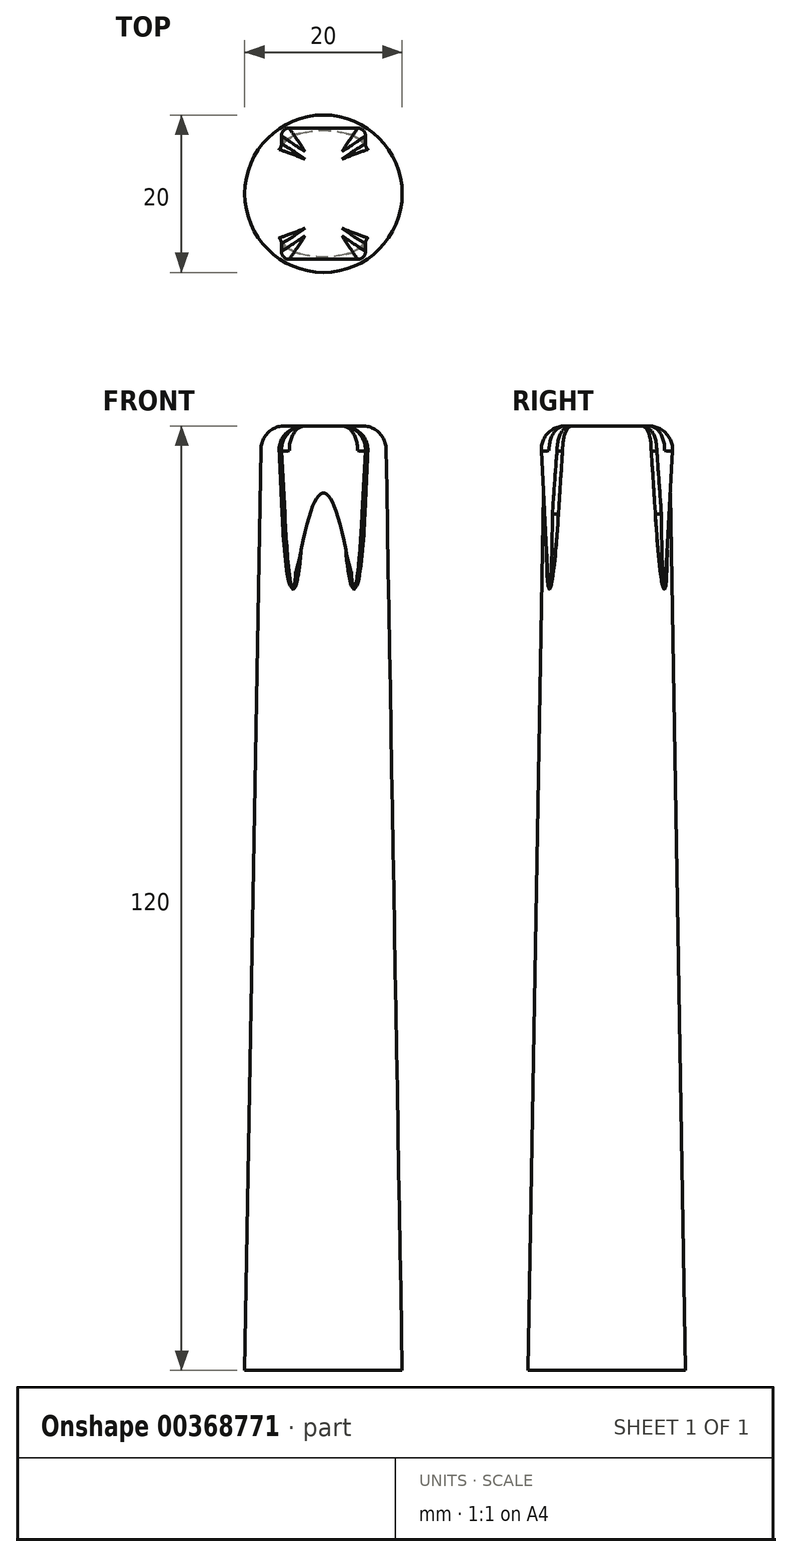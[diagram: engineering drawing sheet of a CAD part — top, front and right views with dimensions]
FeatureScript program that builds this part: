
annotation { "Feature Type Name" : "Feature", "Feature Type Description" : "" }
export const myFeature = defineFeature(function(context is Context, id is Id, definition is map)
    precondition{}
    {
        {
            var Q0;
            Q0=qCreatedBy(makeId("Top.planeOp"),FACE);
            var sketch = newSketch(context, id + "F0", { "sketchPlane" : qUnion([Q0])});
            skCircle(sketch, "E0", {"center": v(0, 0) * mm, "radius": 10 * mm});
            skSolve(sketch);
        }
        {
            var Q0;
            Q0 = qSketchRegion(id + "F0", true);
            extrude(context, id + "F1", {"entities" : qUnion([Q0]), "depth" : 120 * mm, "hasDraft" : true, "draftAngle" : 1 * degree, "draftPullDirection" : true});
        }
        {
            var Q0;
            Q0=makeQuery(id+"F1.opExtrude","CAP_FACE",FACE,{"disambiguationData":[OSD([sQuery(id+"F0.wireOp",EDGE,"E0")])],"isStart":false});
            var sketch = newSketch(context, id + "F2", { "sketchPlane" : qUnion([Q0])});
            skCircle(sketch, "E1.0", {"center": v(0, 0) * mm, "radius": 7.9 * mm});
            skLineSegment(sketch, "E2.bottom", {"start": v(5.5, 8.5) * mm, "end": v(-5.5, 8.5) * mm});
            skLineSegment(sketch, "E2.top", {"start": v(5.5, -8.5) * mm, "end": v(-5.5, -8.5) * mm});
            skLineSegment(sketch, "E2.left", {"start": v(5.5, 8.5) * mm, "end": v(5.5, -8.5) * mm});
            skLineSegment(sketch, "E2.right", {"start": v(-5.5, 8.5) * mm, "end": v(-5.5, -8.5) * mm});
            skSolve(sketch);
        }
        {
            var Q0;
            {var subQ5=sQuery(id+"F2.wireOp",EDGE,"E2.bottom");Q0=makeQuery(id+"F2.imprint","IMPRINT",FACE,{"disambiguationData":[TD([[makeQuery(id+"F2.imprint","IMPRINT",EDGE,{"derivedFrom":subQ5}),1.0]])]});}
            var Q1;
            {var subQ0=sQuery(id+"F2.wireOp",EDGE,"E2.right");var subQ1=sQuery(id+"F2.wireOp",EDGE,"E1.0");var subQ2=makeQuery(id+"F2.imprint","INTERSECT",VERTEX,{"disambiguationData":[OD(0.0)],"derivedFrom":[subQ1,subQ0]});Q1=makeQuery(id+"F2.imprint","IMPRINT",FACE,{"disambiguationData":[TD([[makeQuery(id+"F2.imprint","IMPRINT",EDGE,{"disambiguationData":[TD([[subQ2,1.0]])],"derivedFrom":subQ1}),1.0]])]});}
            var Q2;
            {var subQ5=sQuery(id+"F2.wireOp",EDGE,"E2.top");Q2=makeQuery(id+"F2.imprint","IMPRINT",FACE,{"disambiguationData":[TD([[makeQuery(id+"F2.imprint","IMPRINT",EDGE,{"derivedFrom":subQ5}),-1.0]])]});}
            extrude(context, id + "F3", {"entities" : qUnion([Q0, Q1, Q2]), "operationType" : NewBodyOperationType.ADD, "oppositeDirection" : true, "depth" : 25 * mm, "hasDraft" : true, "draftAngle" : 3 * degree, "draftPullDirection" : true});
        }
        {
            var Q0;
            {var subQ0=sQuery(id+"F0.wireOp",EDGE,"E0");var subQ1=sQuery(id+"F2.wireOp",EDGE,"E2.right");Q0=makeQuery(id+"F3.boolean.opBoolean","SPLIT",EDGE,{"disambiguationData":[TD([makeQuery(id+"F3.opExtrude","SWEPT_FACE",FACE,{"disambiguationData":[OSD([subQ1])]})])],"derivedFrom":makeQuery(id+"F1.opExtrude","CAP_EDGE",EDGE,{"disambiguationData":[OSD([subQ0])],"isStart":false})});}
            var Q1;
            Q1=makeQuery(id+"F3.boolean.opBoolean","MERGE",FACE,{"derivedFrom":[makeQuery(id+"F1.opExtrude","CAP_FACE",FACE,{"disambiguationData":[OSD([sQuery(id+"F0.wireOp",EDGE,"E0")])],"isStart":false}),makeQuery(id+"F3.opExtrude","CAP_FACE",FACE,{"disambiguationData":[OSD([sQuery(id+"F2.wireOp",EDGE,"E2.bottom"),sQuery(id+"F2.wireOp",EDGE,"E2.top"),sQuery(id+"F2.wireOp",EDGE,"E2.left"),sQuery(id+"F2.wireOp",EDGE,"E2.right")])],"isStart":true})]});
            fillet(context, id + "F4", {"entities" : qUnion([Q0, Q1]), "radius" : 3 * mm, "tangentPropagation" : true, "allowEdgeOverflow" : false});
        }
        {
            var Q0;
            {var subQ0=sQuery(id+"F2.wireOp",EDGE,"E2.top");var subQ1=sQuery(id+"F2.wireOp",EDGE,"E2.right");Q0=makeQuery(id+"F4.opFillet","BLEND_EDGE",EDGE,{"blendedFrom":[makeQuery(id+"F3.opExtrude","CAP_EDGE",EDGE,{"disambiguationData":[OSD([subQ0])],"isStart":true}),makeQuery(id+"F3.boolean.opBoolean","SPLIT",EDGE,{"disambiguationData":[TD([makeQuery(id+"F3.opExtrude","SWEPT_FACE",FACE,{"disambiguationData":[OSD([subQ0])]})])],"derivedFrom":makeQuery(id+"F3.opExtrude","CAP_EDGE",EDGE,{"disambiguationData":[OSD([subQ1])],"isStart":true})})],"blendedInto":[]});}
            var Q1;
            {var subQ0=sQuery(id+"F2.wireOp",EDGE,"E2.top");var subQ1=sQuery(id+"F2.wireOp",EDGE,"E2.left");Q1=makeQuery(id+"F4.opFillet","BLEND_EDGE",EDGE,{"blendedFrom":[makeQuery(id+"F3.opExtrude","CAP_EDGE",EDGE,{"disambiguationData":[OSD([subQ0])],"isStart":true}),makeQuery(id+"F3.boolean.opBoolean","SPLIT",EDGE,{"disambiguationData":[TD([makeQuery(id+"F3.opExtrude","SWEPT_FACE",FACE,{"disambiguationData":[OSD([subQ0])]})])],"derivedFrom":makeQuery(id+"F3.opExtrude","CAP_EDGE",EDGE,{"disambiguationData":[OSD([subQ1])],"isStart":true})})],"blendedInto":[]});}
            var Q2;
            {var subQ0=sQuery(id+"F2.wireOp",EDGE,"E2.bottom");var subQ2=sQuery(id+"F2.wireOp",EDGE,"E2.right");Q2=makeQuery(id+"F4.opFillet","BLEND_EDGE",EDGE,{"blendedFrom":[makeQuery(id+"F3.opExtrude","CAP_EDGE",EDGE,{"disambiguationData":[OSD([subQ0])],"isStart":true}),makeQuery(id+"F3.boolean.opBoolean","SPLIT",EDGE,{"disambiguationData":[TD([makeQuery(id+"F3.opExtrude","SWEPT_FACE",FACE,{"disambiguationData":[OSD([subQ0])]})])],"derivedFrom":makeQuery(id+"F3.opExtrude","CAP_EDGE",EDGE,{"disambiguationData":[OSD([subQ2])],"isStart":true})})],"blendedInto":[]});}
            var Q3;
            {var subQ0=sQuery(id+"F2.wireOp",EDGE,"E2.bottom");var subQ2=sQuery(id+"F2.wireOp",EDGE,"E2.left");Q3=makeQuery(id+"F4.opFillet","BLEND_EDGE",EDGE,{"blendedFrom":[makeQuery(id+"F3.opExtrude","CAP_EDGE",EDGE,{"disambiguationData":[OSD([subQ0])],"isStart":true}),makeQuery(id+"F3.boolean.opBoolean","SPLIT",EDGE,{"disambiguationData":[TD([makeQuery(id+"F3.opExtrude","SWEPT_FACE",FACE,{"disambiguationData":[OSD([subQ0])]})])],"derivedFrom":makeQuery(id+"F3.opExtrude","CAP_EDGE",EDGE,{"disambiguationData":[OSD([subQ2])],"isStart":true})})],"blendedInto":[]});}
            var Q4;
            {var subQ0=sQuery(id+"F0.wireOp",EDGE,"E0");var subQ2=sQuery(id+"F2.wireOp",EDGE,"E2.left");var subQ3=makeQuery(id+"F3.opExtrude","SWEPT_FACE",FACE,{"disambiguationData":[OSD([subQ2])]});var subQ5=sQuery(id+"F2.wireOp",EDGE,"E2.bottom");Q4=makeQuery(id+"F4.opFillet","BLEND_EDGE",EDGE,{"blendedFrom":[makeQuery(id+"F3.boolean.opBoolean","SPLIT",EDGE,{"disambiguationData":[TD([makeQuery(id+"F3.opExtrude","SWEPT_FACE",FACE,{"disambiguationData":[OSD([subQ5])]})])],"derivedFrom":makeQuery(id+"F3.opExtrude","CAP_EDGE",EDGE,{"disambiguationData":[OSD([subQ2])],"isStart":true})}),makeQuery(id+"F3.boolean.opBoolean","SPLIT",EDGE,{"disambiguationData":[TD([subQ3])],"derivedFrom":makeQuery(id+"F1.opExtrude","CAP_EDGE",EDGE,{"disambiguationData":[OSD([subQ0])],"isStart":false})})],"blendedInto":[]});}
            var Q5;
            {var subQ0=sQuery(id+"F0.wireOp",EDGE,"E0");var subQ3=sQuery(id+"F2.wireOp",EDGE,"E2.right");var subQ4=sQuery(id+"F2.wireOp",EDGE,"E2.top");var subQ6=makeQuery(id+"F3.opExtrude","SWEPT_FACE",FACE,{"disambiguationData":[OSD([subQ3])]});Q5=makeQuery(id+"F4.opFillet","BLEND_EDGE",EDGE,{"blendedFrom":[makeQuery(id+"F3.boolean.opBoolean","SPLIT",EDGE,{"disambiguationData":[TD([makeQuery(id+"F3.opExtrude","SWEPT_FACE",FACE,{"disambiguationData":[OSD([subQ4])]})])],"derivedFrom":makeQuery(id+"F3.opExtrude","CAP_EDGE",EDGE,{"disambiguationData":[OSD([subQ3])],"isStart":true})}),makeQuery(id+"F3.boolean.opBoolean","SPLIT",EDGE,{"disambiguationData":[TD([subQ6])],"derivedFrom":makeQuery(id+"F1.opExtrude","CAP_EDGE",EDGE,{"disambiguationData":[OSD([subQ0])],"isStart":false})})],"blendedInto":[]});}
            var Q6;
            {var subQ0=sQuery(id+"F0.wireOp",EDGE,"E0");var subQ2=sQuery(id+"F2.wireOp",EDGE,"E2.left");var subQ3=makeQuery(id+"F3.opExtrude","SWEPT_FACE",FACE,{"disambiguationData":[OSD([subQ2])]});var subQ5=sQuery(id+"F2.wireOp",EDGE,"E2.top");Q6=makeQuery(id+"F4.opFillet","BLEND_EDGE",EDGE,{"blendedFrom":[makeQuery(id+"F3.boolean.opBoolean","SPLIT",EDGE,{"disambiguationData":[TD([makeQuery(id+"F3.opExtrude","SWEPT_FACE",FACE,{"disambiguationData":[OSD([subQ5])]})])],"derivedFrom":makeQuery(id+"F3.opExtrude","CAP_EDGE",EDGE,{"disambiguationData":[OSD([subQ2])],"isStart":true})}),makeQuery(id+"F3.boolean.opBoolean","SPLIT",EDGE,{"disambiguationData":[TD([subQ3])],"derivedFrom":makeQuery(id+"F1.opExtrude","CAP_EDGE",EDGE,{"disambiguationData":[OSD([subQ0])],"isStart":false})})],"blendedInto":[]});}
            var Q7;
            {var subQ0=sQuery(id+"F0.wireOp",EDGE,"E0");var subQ3=sQuery(id+"F2.wireOp",EDGE,"E2.right");var subQ4=sQuery(id+"F2.wireOp",EDGE,"E2.bottom");var subQ6=makeQuery(id+"F3.opExtrude","SWEPT_FACE",FACE,{"disambiguationData":[OSD([subQ3])]});Q7=makeQuery(id+"F4.opFillet","BLEND_EDGE",EDGE,{"blendedFrom":[makeQuery(id+"F3.boolean.opBoolean","SPLIT",EDGE,{"disambiguationData":[TD([makeQuery(id+"F3.opExtrude","SWEPT_FACE",FACE,{"disambiguationData":[OSD([subQ4])]})])],"derivedFrom":makeQuery(id+"F3.opExtrude","CAP_EDGE",EDGE,{"disambiguationData":[OSD([subQ3])],"isStart":true})}),makeQuery(id+"F3.boolean.opBoolean","SPLIT",EDGE,{"disambiguationData":[TD([subQ6])],"derivedFrom":makeQuery(id+"F1.opExtrude","CAP_EDGE",EDGE,{"disambiguationData":[OSD([subQ0])],"isStart":false})})],"blendedInto":[]});}
            fillet(context, id + "F5", {"entities" : qUnion([Q0, Q1, Q2, Q3, Q4, Q5, Q6, Q7]), "radius" : 1 * mm, "tangentPropagation" : true, "allowEdgeOverflow" : false});
        }
    });
